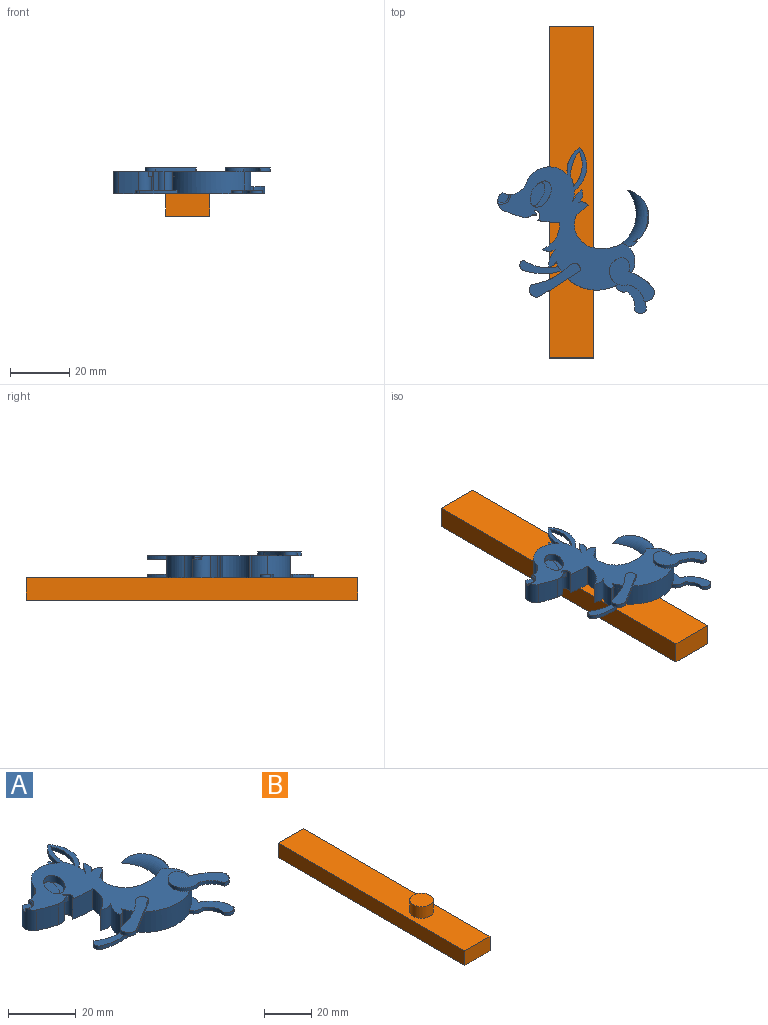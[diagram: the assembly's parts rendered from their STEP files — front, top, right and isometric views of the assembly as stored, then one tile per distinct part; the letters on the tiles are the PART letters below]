
ASSEMBLY  parts=2 mates=1
PART A: 72 faces, bbox 53.6x56.1x10.7 mm
  f0: plane 48.16x46.29mm, normal (0,0,1), area 659.5mm2, adj f1,f3,f4,f5,f7,f8,f9,f10
  f1: cylinder r=49.19mm len=7.65mm, axis (0,0,-1), area 57.6mm2, adj f0,f2,f13,f67
  f2: plane 56.08x51.01mm, normal (0,0,-1), area 853.6mm2, adj f1,f3,f4,f7,f8,f9,f10,f11
  f3: cylinder r=8.39mm len=16.03mm, axis (0,0,-1), area 150.1mm2, adj f0,f2,f10,f50,f51,f60,f61,f65
  f4: cylinder r=8.39mm len=7.5mm, axis (0,0,-1), area 35.8mm2, adj f0,f2,f9,f49,f51,f59,f61,f62
  f5: extruded ~8.85x7.08mm, area 51.1mm2, adj f0,f6,f54,f55
  f6: plane 8.86x6.22mm, normal (0,0,1), area 19.7mm2, adj f5,f55
  f7: cylinder r=6.61mm len=11.03mm, axis (0,0,-1), area 95.8mm2, adj f0,f2,f8,f17,f34,f40,f44,f45
  f8: cylinder r=14.52mm len=24.49mm, axis (0,0,-1), area 216.4mm2, adj f0,f2,f7,f16,f22,f34,f35,f36
  f9: cylinder r=12.15mm len=7.5mm, axis (0,0,-1), area 38.4mm2, adj f0,f2,f4,f21
  f10: cylinder r=5.71mm len=7.77mm, axis (0,0,-1), area 66mm2, adj f0,f2,f3,f11,f56,f57,f58
  f11: cylinder r=3.41mm len=7.5mm, axis (0,0,-1), area 48.6mm2, adj f0,f2,f10,f12,f56,f57,f58
  f12: cylinder r=49.19mm len=7.5mm, axis (0,0,-1), area 53.9mm2, adj f0,f2,f11,f66
  f13: cylinder r=9.43mm len=9.04mm, axis (0,0,-1), area 86.3mm2, adj f0,f1,f2,f14
  f14: cylinder r=3.89mm len=7.5mm, axis (0,0,-1), area 34.9mm2, adj f0,f2,f13,f15
  f15: cylinder r=7.33mm len=7.5mm, axis (0,0,-1), area 50mm2, adj f0,f2,f14,f16
  f16: cylinder r=2.81mm len=7.5mm, axis (0,0,-1), area 25.2mm2, adj f0,f2,f8,f15
  f17: cylinder r=13.61mm len=10.72mm, axis (0,0,-1), area 83.2mm2, adj f0,f2,f7,f18,f71
  f18: cylinder r=7.93mm len=11.12mm, axis (0,0,-1), area 102.9mm2, adj f0,f2,f17,f19
  f19: cylinder r=31.19mm len=7.5mm, axis (0,0,-1), area 35.2mm2, adj f0,f2,f18,f20
  f20: cylinder r=2.32mm len=7.5mm, axis (0,0,-1), area 29.5mm2, adj f0,f2,f19,f21
  f21: cylinder r=3.73mm len=7.5mm, axis (0,0,-1), area 38mm2, adj f0,f2,f9,f20
  f22: plane 12.99x8.38mm, normal (0,0,-1), area 45.2mm2, adj f8,f24,f25,f26
  f23: cylinder r=1.94mm len=3.32mm, axis (0,0,-1), area 6.7mm2, adj f0,f24,f26,f27
  f24: cylinder r=23.44mm len=13.26mm, axis (0,0,-1), area 18.9mm2, adj f0,f22,f23,f25,f27
  f25: cylinder r=2.5mm len=4.19mm, axis (0,0,-1), area 8.6mm2, adj f22,f24,f26,f27
  f26: cylinder r=896.7mm len=13.55mm, axis (0,0,-1), area 20mm2, adj f0,f22,f23,f25,f27
  f27: plane 17.23x11.45mm, normal (0,0,1), area 63.8mm2, adj f23,f24,f25,f26
  f28: cylinder r=3.48mm len=4.71mm, axis (0,0,-1), area 7mm2, adj f0,f29,f32,f33
  f29: cylinder r=4.71mm len=9.43mm, axis (0,0,-1), area 20.4mm2, adj f0,f28,f30,f33,f34
  f30: cylinder r=7.09mm len=5.6mm, axis (0,0,-1), area 10.4mm2, adj f29,f31,f33,f34
  f31: cylinder r=3.01mm len=4.77mm, axis (0,0,-1), area 8.8mm2, adj f30,f32,f33,f34
  f32: cylinder r=20.06mm len=8.13mm, axis (0,0,-1), area 12.3mm2, adj f0,f28,f31,f33,f34
  f33: plane 15.15x14.81mm, normal (0,0,1), area 95mm2, adj f28,f29,f30,f31,f32
  f34: plane 12.23x9.73mm, normal (0,0,-1), area 48.8mm2, adj f7,f8,f29,f30,f31,f32
  f35: cylinder r=14.32mm len=11.69mm, axis (0,0,-1), area 15.3mm2, adj f2,f8,f37,f38
  f36: cylinder r=20.32mm len=12.63mm, axis (0,0,-1), area 16.1mm2, adj f2,f8,f37,f38
  f37: cylinder r=1.82mm len=3.47mm, axis (0,0,-1), area 5.8mm2, adj f2,f35,f36,f38
  f38: plane 13.9x4.61mm, normal (0,0,1), area 31.7mm2, adj f8,f35,f36,f37
  f39: cylinder r=2.94mm len=3.77mm, axis (0,0,-1), area 5.9mm2, adj f2,f8,f41,f44
  f40: cylinder r=4.37mm len=3.3mm, axis (0,0,-1), area 4.3mm2, adj f2,f7,f43,f44
  f41: cylinder r=5.96mm len=6.25mm, axis (0,0,-1), area 9mm2, adj f2,f39,f42,f44
  f42: cylinder r=2.29mm len=3.97mm, axis (0,0,-1), area 6mm2, adj f2,f41,f43,f44
  f43: cylinder r=9.37mm len=9.04mm, axis (0,0,-1), area 14.3mm2, adj f2,f40,f42,f44
  f44: plane 13.48x10.36mm, normal (0,0,1), area 49.8mm2, adj f7,f8,f39,f40,f41,f42,f43
  f45: cylinder r=4.32mm len=2.92mm, axis (0,0,-1), area 8.7mm2, adj f2,f7,f46,f71
  f46: cylinder r=2.01mm len=2.43mm, axis (0,0,-1), area 3.2mm2, adj f2,f45,f47,f71
  f47: cylinder r=9.34mm len=17.5mm, axis (0,0,-1), area 51.5mm2, adj f2,f46,f48,f71
  f48: plane 7x1.21mm, normal (0,0,1), area 1.5mm2, adj f47,f71
  f49: cylinder r=10.04mm len=14.58mm, axis (0,0,1), area 20.6mm2, adj f0,f4,f50,f51
  f50: cylinder r=10.04mm len=9.02mm, axis (0,0,1), area 13.1mm2, adj f0,f3,f49,f51
  f51: plane 14.58x6.65mm, normal (0,0,-1), area 33.4mm2, adj f3,f4,f49,f50,f62,f64,f65
  f52: cylinder r=5mm len=10mm, axis (0,0,-1), area 188.5mm2, adj f2,f53
  f53: plane 10x10mm, normal (0,0,-1), area 78.5mm2, adj f52
  f54: plane 7.87x4.92mm, normal (0,0,1), area 25.6mm2, adj f5,f55
  f55: extruded ~7.87x4.06mm, area 13.7mm2, adj f5,f6,f54
  f56: cylinder r=2.38mm len=3.74mm, axis (0,0,1), area 4mm2, adj f10,f11,f57,f58
  f57: plane 3.74x3.36mm, normal (0,0,1), area 8.9mm2, adj f10,f11,f56
  f58: torus R=2.9mm, axis (0,0,1), area 4.8mm2, adj f0,f10,f11,f56
  f59: cylinder r=10.14mm len=14.57mm, axis (0,0,-1), area 20.5mm2, adj f2,f4,f60,f61
  f60: cylinder r=9.66mm len=9.05mm, axis (0,0,-1), area 13.2mm2, adj f2,f3,f59,f61
  f61: plane 14.57x6.64mm, normal (0,0,1), area 33.5mm2, adj f3,f4,f59,f60,f62,f63,f65
  f62: cylinder r=10.37mm len=11.89mm, axis (0,0,1), area 33.3mm2, adj f0,f2,f4,f51,f61,f63,f64,f65
  f63: cylinder r=13.91mm len=8.46mm, axis (0,0,1), area 11.4mm2, adj f2,f61,f62,f65
  f64: cylinder r=13.91mm len=8.46mm, axis (0,0,1), area 11.4mm2, adj f0,f51,f62,f65
  f65: cylinder r=6.06mm len=7.5mm, axis (0,0,1), area 13.4mm2, adj f0,f2,f3,f51,f61,f62,f63,f64
  f66: cylinder r=3.44mm len=7.5mm, axis (0,0,1), area 37.6mm2, adj f0,f2,f12,f67,f68,f69,f70
  f67: cylinder r=1.89mm len=7.5mm, axis (0,0,1), area 34.2mm2, adj f0,f1,f2,f66
  f68: plane 1.75x1.64mm, normal (0,-1,0), area 2.9mm2, adj f0,f66,f69,f70
  f69: plane 1.75x1.09mm, normal (0.79,0.61,0), area 2.4mm2, adj f0,f66,f68,f70
  f70: plane 1.64x1.09mm, normal (0,0,-1), area 0.8mm2, adj f66,f68,f69
  f71: torus R=16.62mm, axis (0,0,1), area 87.3mm2, adj f2,f7,f17,f45,f46,f47,f48
PART B: 8 faces, bbox 15x112x13.5 mm
  f0: plane 112x7.5mm, normal (1,0,0), area 840mm2, adj f1,f3,f4,f5
  f1: plane 15x7.5mm, normal (0,1,0), area 112.5mm2, adj f0,f2,f4,f5
  f2: plane 112x7.5mm, normal (-1,0,0), area 840mm2, adj f1,f3,f4,f5
  f3: plane 15x7.5mm, normal (0,-1,0), area 112.5mm2, adj f0,f2,f4,f5
  f4: plane 112x15mm, normal (0,0,1), area 1601.5mm2, adj f0,f1,f2,f3,f6
  f5: plane 112x15mm, normal (0,0,-1), area 1680mm2, adj f0,f1,f2,f3
  f6: cylinder r=5mm len=10mm, axis (0,0,-1), area 188.5mm2, adj f4,f7
  f7: plane 10x10mm, normal (0,0,1), area 78.5mm2, adj f6
PLACE A t=(0,33.81,7.5)mm
PLACE B t=(0,48.81,0)mm fixed
MATE fastened A.f52 <-> B.f6  axis (0,0,-1) through (0,26.31,13.5)mm
